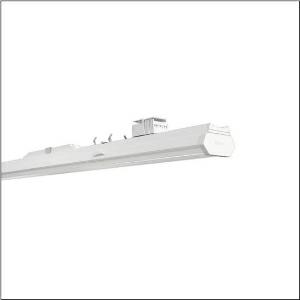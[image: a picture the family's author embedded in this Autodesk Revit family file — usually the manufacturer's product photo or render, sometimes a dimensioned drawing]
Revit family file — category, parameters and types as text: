
# Revit family: licross_r__11_protected_ho_51tp12mn4f5m_a747
name_source: partatom
category: Lighting Fixtures
units: mm (PartAtom-declared; Revit-internal decimal feet)

## family parameters
Cut with Voids When Loaded = No
Host = Face
Light Source = No
Part Type = Normal
Room Calculation Point = No
Round Connector Dimension = Use Diameter
Shared = No

## types (1)
- --- (1 x LED, 15820 lm, 87.4 W, 4000K)
    Apparent Load = 87 VA
    CIE Flux Codes = 70 91 97 98 100
    Color Rendering = 80
    Color Temperature = 4000K
    Default Elevation = 1800 mm
    Description = Licross® 11 Protected HO, luminaire insert, of sheet steel, galvanised, coil coated, white, length: 1.500mm, width: 90mm, height: 101mm, LED rated luminous flux: 15.820lm, light colour: 840, control gear: ON/OFF Multilumen, with plug, 3-pole, with phase selection, mains connection: 220..240V, AC, 50/60Hz, rated input power: 87W, halogen-free wiring, primary light control with lens, of plastic, primary optical cover: cover, of PMMA, light emission: direct distribution, primary light characteristic: symmetric, protection rating (complete): IP64, insulation class (complete): insulation class I (protective earthing), certification: CE, ENEC, VDE, UKCA, protection symbol: D if used in an environment with conductive dust loads with corresponding accessories, impact resistance: IK06, permissible ambient temperature for indoor applications: -35..+35°C, corresponds to IFS (International Featured Standards) requirements for safety and quality in the food industry, reducing of maximum allowable ambient temperature of 5°C with ceiling mounting, LABS conformity tested according to VDMA 24364:2018-05, packaging unit: 1 piece
    Height = 92 mm
    Lamp = 1 x LED
    Lamp Light Flux = 15820 lm
    Lamp Power = 87.4 W
    Lamp count = 1
    Length = 1500 mm
    Luminous efficacy = 181 lm/W
    Manufacturer = Siteco
    ModVariant = No
    Model = 51TP12MN4F5M
    Mounting Place = Ceiling
    Mounting Type = Pendant
    Number of Poles = 1
    OnlyDefault = Yes
    Power Factor = 1
    Product Name = Licross® 11 Protected HO
    Product group = luminaire insert
    ProductGroupID = 902
    Protection Class = Protection class I
    Protection Degree = IP 64
    RLX_Detail_Level = 1
    RLX_Emergency_Light_Flux = 0 lm
    RLX_Emergency_Type = 0
    RLX_Emergency_Type_DB = No
    RlxData = <blob elided: 22009 chars, md5=9bbecb41>
    Socket = socket
    Standby Power = 0 W
    System Light Flux = 15820 lm
    System Power = 87 W
    Type Comments = factory setting: luminous flux: 100 % | (A | C | E) | 203 mA
    Type Image = l_1256148.jpg
    URL = http://relux.com
    VarID = @adj_085972
    Voltage = 0 V
    Weight = 0.00 kg
    Width = 88 mm

## geometry (parser evidence)
native form markers: Blend x4, Sweep x12
no freeform markers — native parametric forms only
